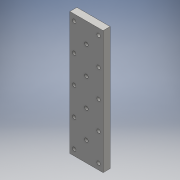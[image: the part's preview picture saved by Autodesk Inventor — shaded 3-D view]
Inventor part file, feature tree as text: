
AUTODESK INVENTOR PART (.ipt)
format: ipt  version: 2016 (Build 200138000, 138)  size: 136,192 bytes
history: native  units: mm
features: extrude x1, sketch x1
ambient origin geometry x8: Origin, YZ Plane, XZ Plane, XY Plane, X Axis, Y Axis, Z Axis, Center Point
bodies: Body1 (feature_tree)
feature tree (2):
  extrude  "Extrusion2"  Depth=6.39mm
  sketch  "Sketch1"  dims[d0=20.9mm d1=3.175mm d2=19.8mm d3=3.175mm d4=19.14mm d5=3.175mm d6=18.7mm d7=3.175mm d8=25.0mm d9=25.0mm d10=25.0mm d11=15.0mm d12=15.0mm d13=18.0mm d14=18.0mm d15=1.0mm d16=1.0mm d17=1.0mm d18=1.0mm d19=3.175mm d20=4.0mm d23=6.39mm d24=0.0mm]
